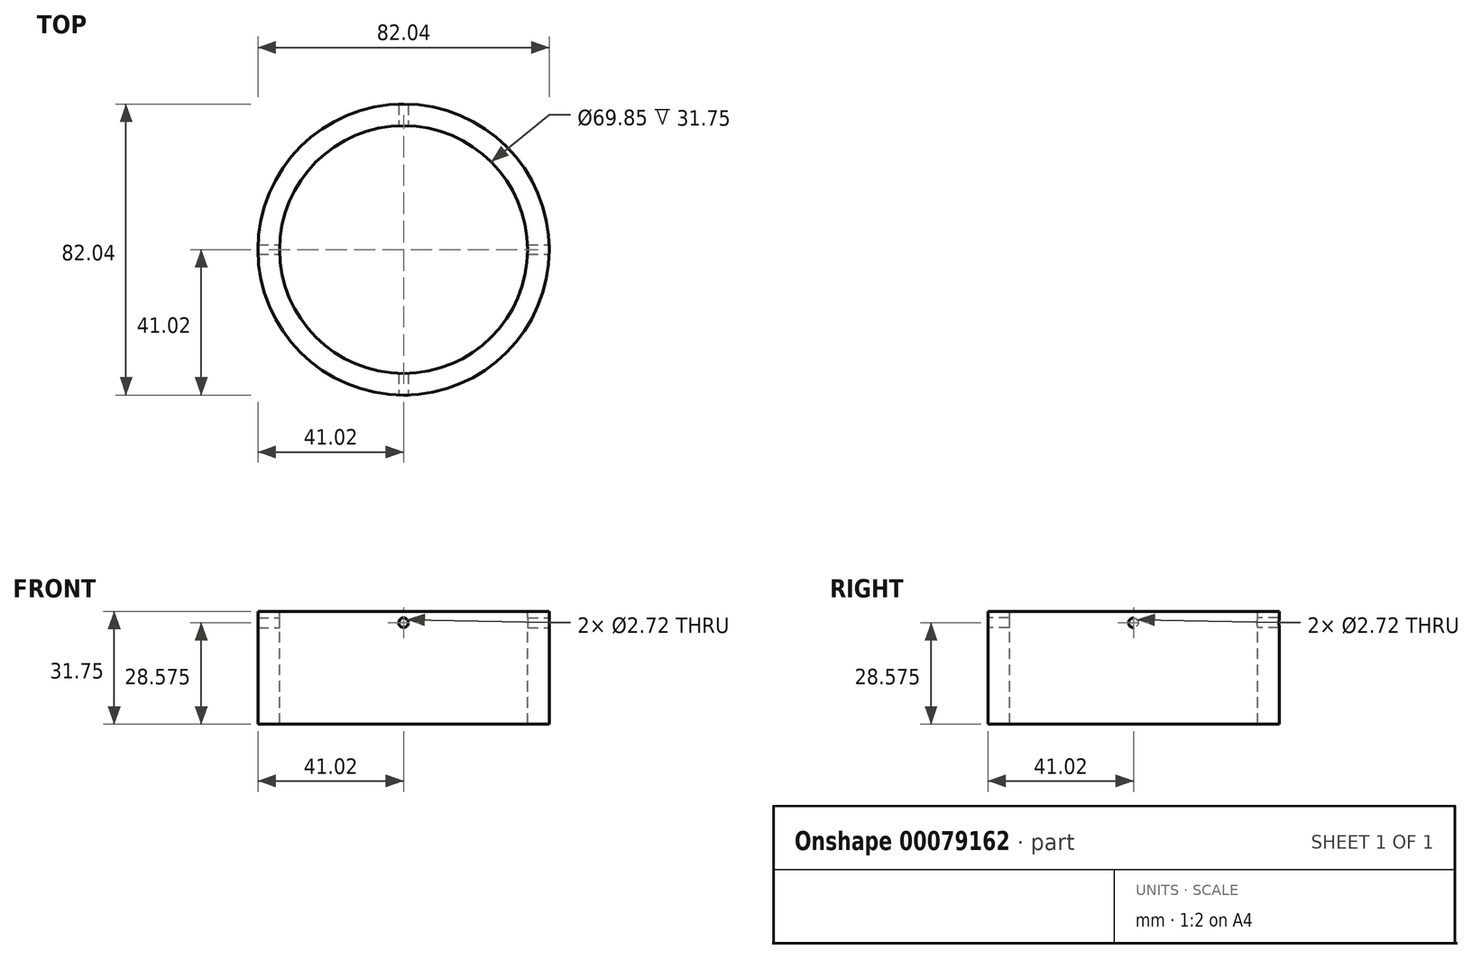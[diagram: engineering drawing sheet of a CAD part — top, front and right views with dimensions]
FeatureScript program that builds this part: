
annotation { "Feature Type Name" : "Feature", "Feature Type Description" : "" }
export const myFeature = defineFeature(function(context is Context, id is Id, definition is map)
    precondition{}
    {
        {
            var Q0;
            Q0=qCreatedBy(makeId("Top.planeOp"),FACE);
            var sketch = newSketch(context, id + "F0", { "sketchPlane" : qUnion([Q0])});
            skCircle(sketch, "E0", {"center": v(0, 0) * mm, "radius": 41.02 * mm});
            skSolve(sketch);
        }
        {
            var Q0;
            Q0=makeQuery(id+"F0.imprint","IMPRINT",FACE,{"disambiguationData":[TD([[makeQuery(id+"F0.imprint","IMPRINT",EDGE,{"derivedFrom":sQuery(id+"F0.wireOp",EDGE,"E0")}),1.0]])]});
            extrude(context, id + "F1", {"entities" : qUnion([Q0]), "depth" : 31.75 * mm});
        }
        {
            var Q0;
            Q0=makeQuery(id+"F1.opExtrude","CAP_FACE",FACE,{"disambiguationData":[OSD([sQuery(id+"F0.wireOp",EDGE,"E0")])],"isStart":false});
            var sketch = newSketch(context, id + "F2", { "sketchPlane" : qUnion([Q0])});
            skCircle(sketch, "E1", {"center": v(0, 0) * mm, "radius": 34.93 * mm});
            skSolve(sketch);
        }
        {
            var Q0;
            Q0=makeQuery(id+"F2.imprint","IMPRINT",FACE,{"disambiguationData":[TD([[makeQuery(id+"F2.imprint","IMPRINT",EDGE,{"derivedFrom":sQuery(id+"F2.wireOp",EDGE,"E1")}),1.0]])]});
            extrude(context, id + "F3", {"entities" : qUnion([Q0]), "operationType" : NewBodyOperationType.REMOVE, "endBound" : BoundingType.THROUGH_ALL, "oppositeDirection" : true, "depth" : 25.4 * mm});
        }
        {
            var Q0;
            Q0=qCreatedBy(makeId("Front.planeOp"),FACE);
            var sketch = newSketch(context, id + "F4", { "sketchPlane" : qUnion([Q0])});
            skCircle(sketch, "E2", {"center": v(0, 28.57) * mm, "radius": 1.36 * mm});
            skSolve(sketch);
        }
        {
            var Q0;
            Q0 = qSketchRegion(id + "F4", true);
            extrude(context, id + "F5", {"entities" : qUnion([Q0]), "operationType" : NewBodyOperationType.REMOVE, "oppositeDirection" : true, "depth" : 88.9 * mm, "symmetric" : true});
        }
        {
            var Q0;
            Q0=qCreatedBy(makeId("Right.planeOp"),FACE);
            var sketch = newSketch(context, id + "F6", { "sketchPlane" : qUnion([Q0])});
            skCircle(sketch, "E3", {"center": v(0, 28.57) * mm, "radius": 1.36 * mm});
            skSolve(sketch);
        }
        {
            var Q0;
            Q0 = qSketchRegion(id + "F6", true);
            extrude(context, id + "F7", {"entities" : qUnion([Q0]), "operationType" : NewBodyOperationType.REMOVE, "oppositeDirection" : true, "depth" : 88.9 * mm, "symmetric" : true});
        }
    });
